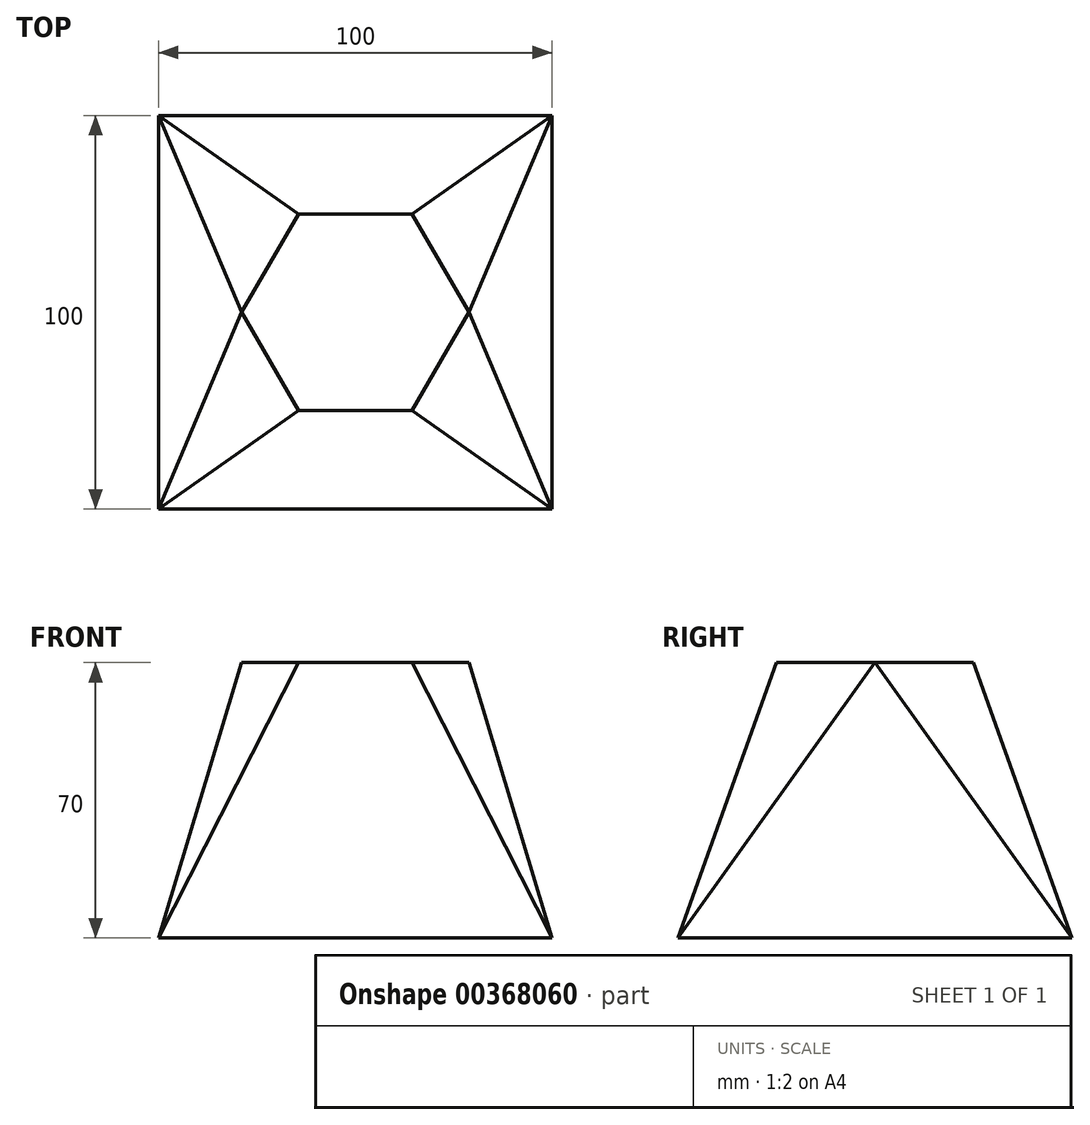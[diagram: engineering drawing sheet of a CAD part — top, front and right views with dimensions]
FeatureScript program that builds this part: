
annotation { "Feature Type Name" : "Feature", "Feature Type Description" : "" }
export const myFeature = defineFeature(function(context is Context, id is Id, definition is map)
    precondition{}
    {
        {
            var Q0;
            Q0=qCreatedBy(makeId("Top.planeOp"),FACE);
            var sketch = newSketch(context, id + "F0", { "sketchPlane" : qUnion([Q0])});
            skLineSegment(sketch, "E0.bottom", {"start": v(-50, 50) * mm, "end": v(50, 50) * mm});
            skLineSegment(sketch, "E0.top", {"start": v(-50, -50) * mm, "end": v(50, -50) * mm});
            skLineSegment(sketch, "E0.left", {"start": v(-50, 50) * mm, "end": v(-50, -50) * mm});
            skLineSegment(sketch, "E0.right", {"start": v(50, 50) * mm, "end": v(50, -50) * mm});
            skSolve(sketch);
        }
        {
            var Q0;
            Q0=qCreatedBy(makeId("Top.planeOp"),FACE);
            cPlane(context, id + "F1", {"entities" : qUnion([Q0]), "cplaneType" : CPlaneType.OFFSET, "offset" : 70 * mm, "width" : 150 * mm, "height" : 150 * mm});
        }
        {
            var Q0;
            Q0=qCreatedBy(id+"F1.planeOp",FACE);
            var sketch = newSketch(context, id + "F2", { "sketchPlane" : qUnion([Q0])});
            skCircle(sketch, "E1.cCircle", {"center": v(0, 0) * mm, "radius": 25 * mm, "construction": true});
            skLineSegment(sketch, "E1.0", {"start": v(14.43, -25) * mm, "end": v(-14.43, -25) * mm});
            skLineSegment(sketch, "E1.1", {"start": v(-14.43, -25) * mm, "end": v(-28.87, 0) * mm});
            skLineSegment(sketch, "E1.2", {"start": v(-28.87, 0) * mm, "end": v(-14.43, 25) * mm});
            skLineSegment(sketch, "E1.3", {"start": v(-14.43, 25) * mm, "end": v(14.43, 25) * mm});
            skLineSegment(sketch, "E1.4", {"start": v(14.43, 25) * mm, "end": v(28.87, 0) * mm});
            skLineSegment(sketch, "E1.5", {"start": v(28.87, 0) * mm, "end": v(14.43, -25) * mm});
            skPoint(sketch, "E1.0.midPoint", {"position": v(0, -25) * mm});
            skLineSegment(sketch, "E2", {"start": v(-14.43, -25) * mm, "end": v(-14.43, 25) * mm});
            skLineSegment(sketch, "E3", {"start": v(14.43, -25) * mm, "end": v(14.43, 25) * mm});
            skSolve(sketch);
        }
        {
            var Q0;
            Q0=makeQuery(id+"F2.imprint","IMPRINT",FACE,{"disambiguationData":[TD([[makeQuery(id+"F2.imprint","IMPRINT",EDGE,{"derivedFrom":sQuery(id+"F2.wireOp",EDGE,"E1.0")}),-1.0]])]});
            var Q1;
            Q1=makeQuery(id+"F0.imprint","IMPRINT",FACE,{"disambiguationData":[TD([[makeQuery(id+"F0.imprint","IMPRINT",EDGE,{"derivedFrom":sQuery(id+"F0.wireOp",EDGE,"E0.bottom")}),-1.0]])]});
            loft(context, id + "F3", {"sheetProfilesArray" : [{ "sheetProfileEntities" : qUnion([Q0]) }, { "sheetProfileEntities" : qUnion([Q1]) }]});
        }
        {
            var Q1;
            Q1=makeQuery(id+"F2.imprint","IMPRINT",FACE,{"disambiguationData":[TD([[makeQuery(id+"F2.imprint","IMPRINT",EDGE,{"derivedFrom":sQuery(id+"F2.wireOp",EDGE,"E1.1")}),-1.0]])]});
            var Q2;
            Q2=makeQuery(id+"F3.opLoft","MID_CAP_VERTEX",VERTEX,{"disambiguationData":[OSD([sQuery(id+"F0.wireOp",EDGE,"E0.top"),sQuery(id+"F0.wireOp",EDGE,"E0.left")])],"capPos":1.0});
            loft(context, id + "F4", {"operationType" : NewBodyOperationType.ADD, "sheetProfilesArray" : [{ "sheetProfileEntities" : qUnion([Q1]) }, { "sheetProfileEntities" : qUnion([Q2]) }]});
        }
        {
            var Q1;
            Q1=makeQuery(id+"F2.imprint","IMPRINT",FACE,{"disambiguationData":[TD([[makeQuery(id+"F2.imprint","IMPRINT",EDGE,{"derivedFrom":sQuery(id+"F2.wireOp",EDGE,"E1.1")}),-1.0]])]});
            var Q2;
            Q2=makeQuery(id+"F3.opLoft","MID_CAP_VERTEX",VERTEX,{"disambiguationData":[OSD([sQuery(id+"F0.wireOp",EDGE,"E0.bottom"),sQuery(id+"F0.wireOp",EDGE,"E0.left")])],"capPos":1.0});
            loft(context, id + "F5", {"operationType" : NewBodyOperationType.ADD, "sheetProfilesArray" : [{ "sheetProfileEntities" : qUnion([Q1]) }, { "sheetProfileEntities" : qUnion([Q2]) }]});
        }
        {
            var Q1;
            Q1=makeQuery(id+"F5.opLoft","SWEPT_FACE",FACE,{"disambiguationData":[OSD([sQuery(id+"F2.wireOp",EDGE,"E1.0"),sQuery(id+"F2.wireOp",EDGE,"E1.1"),sQuery(id+"F2.wireOp",EDGE,"E1.2"),sQuery(id+"F2.wireOp",EDGE,"E2")])]});
            var Q2;
            Q2=makeQuery(id+"F4.opLoft","SWEPT_FACE",FACE,{"disambiguationData":[OSD([sQuery(id+"F2.wireOp",EDGE,"E1.1"),sQuery(id+"F2.wireOp",EDGE,"E1.2"),sQuery(id+"F2.wireOp",EDGE,"E1.3"),sQuery(id+"F2.wireOp",EDGE,"E2")])]});
            var Q3;
            {var subQ0=sQuery(id+"F0.wireOp",EDGE,"E0.left");var subQ1=sQuery(id+"F0.wireOp",EDGE,"E0.bottom");Q3=makeQuery(id+"F5.boolean.opBoolean","MERGE",VERTEX,{"derivedFrom":[makeQuery(id+"F3.opLoft","MID_CAP_VERTEX",VERTEX,{"disambiguationData":[OSD([subQ1,subQ0])],"capPos":1.0}),makeQuery(id+"F5.opLoft","SWEPT_VERTEX",VERTEX,{"disambiguationData":[OSD([subQ1,subQ0,sQuery(id+"F2.wireOp",EDGE,"E1.1"),sQuery(id+"F2.wireOp",EDGE,"E1.2")])]})]});}
            var Q4;
            {var subQ0=sQuery(id+"F0.wireOp",EDGE,"E0.left");var subQ1=sQuery(id+"F0.wireOp",EDGE,"E0.top");Q4=makeQuery(id+"F4.boolean.opBoolean","MERGE",VERTEX,{"derivedFrom":[makeQuery(id+"F3.opLoft","MID_CAP_VERTEX",VERTEX,{"disambiguationData":[OSD([subQ1,subQ0])],"capPos":1.0}),makeQuery(id+"F4.opLoft","SWEPT_VERTEX",VERTEX,{"disambiguationData":[OSD([subQ1,subQ0,sQuery(id+"F2.wireOp",EDGE,"E1.1"),sQuery(id+"F2.wireOp",EDGE,"E1.2")])]})]});}
            loft(context, id + "F6", {"operationType" : NewBodyOperationType.ADD, "sheetProfilesArray" : [{ "sheetProfileEntities" : qUnion([Q1]) }, { "sheetProfileEntities" : qUnion([Q2]) }], "matchConnections" : true, "connections" : [{ "connectionEntities" : qUnion([Q3, Q4]), "connectionEdgeQueries" : qUnion([]), "connectionEdgeParameters" : [] }]});
        }
        {
            var Q1;
            Q1=makeQuery(id+"F2.imprint","IMPRINT",FACE,{"disambiguationData":[TD([[makeQuery(id+"F2.imprint","IMPRINT",EDGE,{"derivedFrom":sQuery(id+"F2.wireOp",EDGE,"E1.4")}),-1.0]])]});
            var Q2;
            Q2=makeQuery(id+"F3.opLoft","MID_CAP_VERTEX",VERTEX,{"disambiguationData":[OSD([sQuery(id+"F0.wireOp",EDGE,"E0.bottom"),sQuery(id+"F0.wireOp",EDGE,"E0.right")])],"capPos":1.0});
            loft(context, id + "F7", {"operationType" : NewBodyOperationType.ADD, "sheetProfilesArray" : [{ "sheetProfileEntities" : qUnion([Q1]) }, { "sheetProfileEntities" : qUnion([Q2]) }]});
        }
        {
            var Q1;
            Q1=makeQuery(id+"F2.imprint","IMPRINT",FACE,{"disambiguationData":[TD([[makeQuery(id+"F2.imprint","IMPRINT",EDGE,{"derivedFrom":sQuery(id+"F2.wireOp",EDGE,"E1.4")}),-1.0]])]});
            var Q2;
            Q2=makeQuery(id+"F3.opLoft","MID_CAP_VERTEX",VERTEX,{"disambiguationData":[OSD([sQuery(id+"F0.wireOp",EDGE,"E0.top"),sQuery(id+"F0.wireOp",EDGE,"E0.right")])],"capPos":1.0});
            loft(context, id + "F8", {"operationType" : NewBodyOperationType.ADD, "sheetProfilesArray" : [{ "sheetProfileEntities" : qUnion([Q1]) }, { "sheetProfileEntities" : qUnion([Q2]) }]});
        }
        {
            var Q1;
            Q1=makeQuery(id+"F8.opLoft","SWEPT_FACE",FACE,{"disambiguationData":[OSD([sQuery(id+"F2.wireOp",EDGE,"E1.3"),sQuery(id+"F2.wireOp",EDGE,"E1.4"),sQuery(id+"F2.wireOp",EDGE,"E1.5"),sQuery(id+"F2.wireOp",EDGE,"E3")])]});
            var Q2;
            Q2=makeQuery(id+"F7.opLoft","SWEPT_FACE",FACE,{"disambiguationData":[OSD([sQuery(id+"F2.wireOp",EDGE,"E1.0"),sQuery(id+"F2.wireOp",EDGE,"E1.4"),sQuery(id+"F2.wireOp",EDGE,"E1.5"),sQuery(id+"F2.wireOp",EDGE,"E3")])]});
            var Q3;
            {var subQ0=sQuery(id+"F0.wireOp",EDGE,"E0.right");var subQ1=sQuery(id+"F0.wireOp",EDGE,"E0.bottom");Q3=makeQuery(id+"F7.boolean.opBoolean","MERGE",VERTEX,{"derivedFrom":[makeQuery(id+"F3.opLoft","MID_CAP_VERTEX",VERTEX,{"disambiguationData":[OSD([subQ1,subQ0])],"capPos":1.0}),makeQuery(id+"F7.opLoft","SWEPT_VERTEX",VERTEX,{"disambiguationData":[OSD([subQ1,subQ0,sQuery(id+"F2.wireOp",EDGE,"E1.3"),sQuery(id+"F2.wireOp",EDGE,"E1.4"),sQuery(id+"F2.wireOp",EDGE,"E3")])]})]});}
            var Q4;
            {var subQ0=sQuery(id+"F0.wireOp",EDGE,"E0.right");var subQ1=sQuery(id+"F0.wireOp",EDGE,"E0.top");Q4=makeQuery(id+"F8.boolean.opBoolean","MERGE",VERTEX,{"derivedFrom":[makeQuery(id+"F3.opLoft","MID_CAP_VERTEX",VERTEX,{"disambiguationData":[OSD([subQ1,subQ0])],"capPos":1.0}),makeQuery(id+"F8.opLoft","SWEPT_VERTEX",VERTEX,{"disambiguationData":[OSD([subQ1,subQ0,sQuery(id+"F2.wireOp",EDGE,"E1.3"),sQuery(id+"F2.wireOp",EDGE,"E1.4"),sQuery(id+"F2.wireOp",EDGE,"E3")])]})]});}
            loft(context, id + "F9", {"operationType" : NewBodyOperationType.ADD, "sheetProfilesArray" : [{ "sheetProfileEntities" : qUnion([Q1]) }, { "sheetProfileEntities" : qUnion([Q2]) }], "matchConnections" : true, "connections" : [{ "connectionEntities" : qUnion([Q3, Q4]), "connectionEdgeQueries" : qUnion([]), "connectionEdgeParameters" : [] }]});
        }
    });
